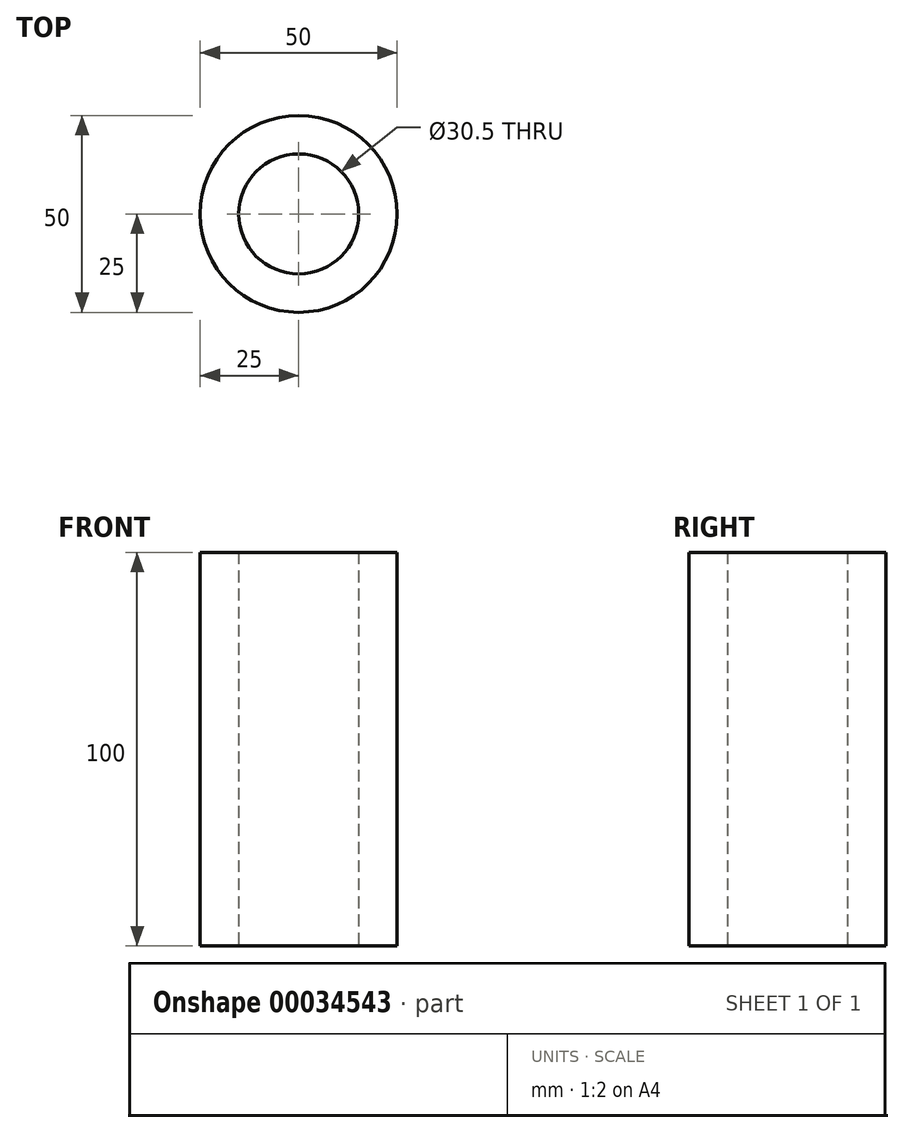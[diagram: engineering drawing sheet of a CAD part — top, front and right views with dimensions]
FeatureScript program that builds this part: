
annotation { "Feature Type Name" : "Feature", "Feature Type Description" : "" }
export const myFeature = defineFeature(function(context is Context, id is Id, definition is map)
    precondition{}
    {
        {
            var Q0;
            Q0=qCreatedBy(makeId("Top.planeOp"),FACE);
            var sketch = newSketch(context, id + "F0", { "sketchPlane" : qUnion([Q0])});
            skCircle(sketch, "E0", {"center": v(0, 0) * mm, "radius": 15.25 * mm});
            skCircle(sketch, "E1", {"center": v(0, 0) * mm, "radius": 25 * mm});
            skSolve(sketch);
        }
        {
            var Q0;
            Q0 = qSketchRegion(id + "F0", true);
            extrude(context, id + "F1", {"entities" : qUnion([Q0]), "depth" : 100 * mm});
        }
    });
